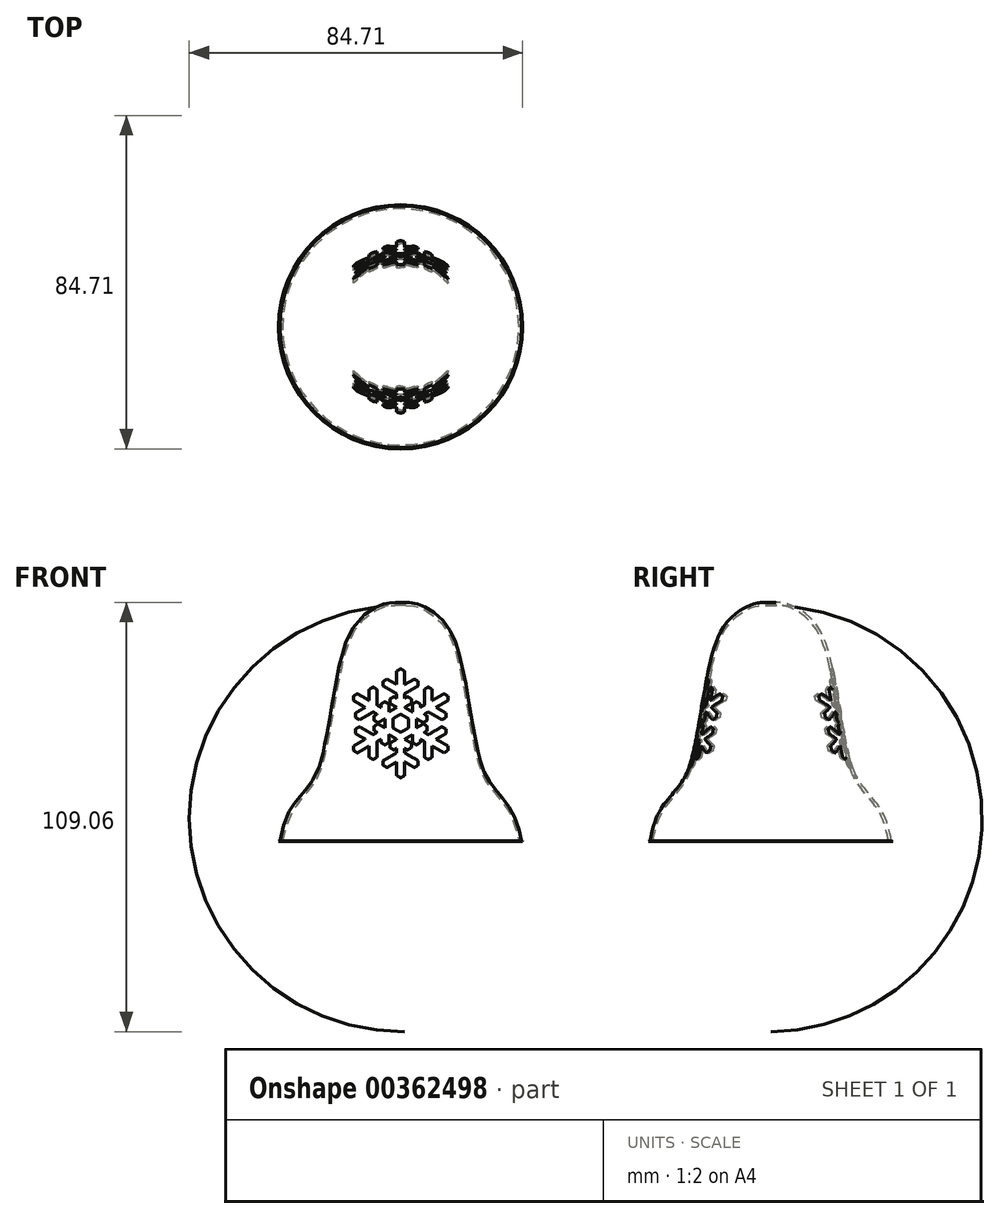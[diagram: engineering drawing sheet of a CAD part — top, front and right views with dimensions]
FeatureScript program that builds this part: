
annotation { "Feature Type Name" : "Feature", "Feature Type Description" : "" }
export const myFeature = defineFeature(function(context is Context, id is Id, definition is map)
    precondition{}
    {
        {
            var Q0;
            Q0=qCreatedBy(makeId("Front.planeOp"),FACE);
            var sketch = newSketch(context, id + "F0", { "sketchPlane" : qUnion([Q0])});
            skLineSegment(sketch, "E0", {"start": v(0, 60.7) * mm, "end": v(0, 0) * mm});
            skLineSegment(sketch, "E1", {"start": v(0, 0) * mm, "end": v(31, 0) * mm});
            skFitSpline(sketch, "E2", {"points": [v(0, 60) * mm, v(4.46, 59.52) * mm, v(9.31, 56.54) * mm, v(14.11, 47.63) * mm, v(19.42, 20.89) * mm, v(23, 13.4) * mm, v(27.43, 7.62) * mm, v(30, 0) * mm], "startDerivative": vector(62.73, 0.31) * mm, "endDerivative": vector(16.94, -75.2) * mm});
            skFitSpline(sketch, "E3.0", {"points": [v(0, 59.5) * mm, v(0.65, 59.5) * mm, v(1.75, 59.5) * mm, v(2.78, 59.42) * mm, v(3.52, 59.28) * mm, v(4.08, 59.13) * mm, v(4.68, 58.91) * mm, v(5.53, 58.55) * mm, v(6.65, 57.95) * mm, v(7.79, 57.18) * mm, v(8.65, 56.47) * mm, v(9.48, 55.71) * mm, v(10.42, 54.66) * mm, v(11.44, 53.13) * mm, v(12.36, 51.27) * mm, v(13.07, 49.37) * mm, v(13.6, 47.61) * mm, v(14.12, 45.67) * mm, v(14.74, 42.95) * mm, v(15.66, 38.18) * mm, v(16.53, 33.06) * mm, v(17.38, 28.15) * mm, v(17.92, 25.29) * mm, v(18.35, 23.2) * mm, v(18.69, 21.73) * mm, v(19.03, 20.4) * mm, v(19.5, 18.82) * mm, v(20.12, 17.15) * mm, v(20.95, 15.49) * mm, v(21.72, 14.28) * mm, v(22.4, 13.36) * mm, v(23.12, 12.44) * mm, v(24.08, 11.28) * mm, v(25.25, 9.86) * mm, v(26.16, 8.67) * mm, v(26.8, 7.72) * mm, v(27.37, 6.76) * mm, v(27.94, 5.54) * mm, v(28.5, 3.94) * mm, v(29, 2.1) * mm, v(29.34, 0.67) * mm, v(29.51, -0.1) * mm]});
            skFitSpline(sketch, "E4.0", {"points": [v(0, 60.7) * mm, v(0.65, 60.7) * mm, v(1.77, 60.7) * mm, v(2.92, 60.61) * mm, v(3.8, 60.45) * mm, v(4.45, 60.27) * mm, v(5.12, 60.03) * mm, v(6.06, 59.63) * mm, v(7.28, 58.98) * mm, v(8.74, 57.98) * mm, v(10.13, 56.78) * mm, v(11.37, 55.4) * mm, v(12.48, 53.73) * mm, v(13.47, 51.74) * mm, v(14.2, 49.76) * mm, v(14.76, 47.94) * mm, v(15.29, 45.95) * mm, v(15.91, 43.2) * mm, v(16.84, 38.39) * mm, v(17.71, 33.26) * mm, v(18.56, 28.36) * mm, v(19.1, 25.52) * mm, v(19.53, 23.45) * mm, v(19.85, 22.02) * mm, v(20.19, 20.72) * mm, v(20.64, 19.2) * mm, v(21.23, 17.62) * mm, v(22, 16.08) * mm, v(22.7, 14.96) * mm, v(23.35, 14.09) * mm, v(24.05, 13.2) * mm, v(25, 12.05) * mm, v(26.19, 10.62) * mm, v(27.32, 9.13) * mm, v(28.3, 7.59) * mm, v(29.06, 6) * mm, v(29.86, 3.72) * mm, v(30.33, 1.72) * mm, v(30.68, 0.15) * mm]});
            skLineSegment(sketch, "E5", {"start": v(30.68, 0.15) * mm, "end": v(31, 0) * mm});
            skLineSegment(sketch, "E6", {"start": v(0, 59.5) * mm, "end": v(0, 59.5) * mm});
            skLineSegment(sketch, "E7.0", {"start": v(1.4, 60.7) * mm, "end": v(1.4, 0) * mm});
            skSolve(sketch);
        }
        {
            var Q0;
            Q0=qCreatedBy(makeId("Front.planeOp"),FACE);
            var sketch = newSketch(context, id + "F1", { "sketchPlane" : qUnion([Q0])});
            skLineSegment(sketch, "E8", {"start": v(0, 0) * mm, "end": v(0, 54.78) * mm, "construction": true});
            skLineSegment(sketch, "E9", {"start": v(-27.16, 30) * mm, "end": v(27.16, 30) * mm, "construction": true});
            skPoint(sketch, "E10", {"position": v(0, 30) * mm});
            skCircle(sketch, "E11.cCircle", {"center": v(0, 30) * mm, "radius": 12 * mm, "construction": true});
            skLineSegment(sketch, "E11.0", {"start": v(-12, 23.07) * mm, "end": v(-12, 36.93) * mm, "construction": true});
            skLineSegment(sketch, "E11.1", {"start": v(-12, 36.93) * mm, "end": v(0, 43.86) * mm, "construction": true});
            skLineSegment(sketch, "E11.2", {"start": v(0, 43.86) * mm, "end": v(12, 36.93) * mm, "construction": true});
            skLineSegment(sketch, "E11.3", {"start": v(12, 36.93) * mm, "end": v(12, 23.07) * mm, "construction": true});
            skLineSegment(sketch, "E11.4", {"start": v(12, 23.07) * mm, "end": v(0, 16.14) * mm, "construction": true});
            skLineSegment(sketch, "E11.5", {"start": v(0, 16.14) * mm, "end": v(-12, 23.07) * mm, "construction": true});
            skPoint(sketch, "E11.0.midPoint", {"position": v(-12, 30) * mm});
            skCircle(sketch, "E12.cCircle", {"center": v(0, 30) * mm, "radius": 2 * mm, "construction": true});
            skLineSegment(sketch, "E12.0", {"start": v(-2, 28.85) * mm, "end": v(-2, 31.15) * mm});
            skLineSegment(sketch, "E12.1", {"start": v(-2, 31.15) * mm, "end": v(0, 32.3) * mm});
            skLineSegment(sketch, "E12.2", {"start": v(0, 32.3) * mm, "end": v(2, 31.15) * mm});
            skLineSegment(sketch, "E12.3", {"start": v(2, 31.15) * mm, "end": v(2, 28.85) * mm});
            skLineSegment(sketch, "E12.4", {"start": v(2, 28.85) * mm, "end": v(0, 27.7) * mm});
            skLineSegment(sketch, "E12.5", {"start": v(0, 27.7) * mm, "end": v(-2, 28.85) * mm});
            skPoint(sketch, "E12.0.midPoint", {"position": v(-2, 30) * mm});
            skPoint(sketch, "E13.0.midPoint", {"position": v(-4, 30) * mm});
            skPoint(sketch, "E14.start.orphan", {"position": v(-1, 30) * mm});
            skLineSegment(sketch, "E15.trimOffspring", {"start": v(1, 36.35) * mm, "end": v(1, 37.5) * mm});
            skPoint(sketch, "E16.MirrorCS.start.orphan", {"position": v(1, 30) * mm});
            skPoint(sketch, "E17.orphan", {"position": v(0, 34.62) * mm});
            skLineSegment(sketch, "E18", {"start": v(1, 43.28) * mm, "end": v(0, 43.86) * mm});
            skPoint(sketch, "E19", {"position": v(1, 38.66) * mm});
            skLineSegment(sketch, "E20", {"start": v(1, 39.81) * mm, "end": v(1, 43.28) * mm});
            skLineSegment(sketch, "E21", {"start": v(1, 38.66) * mm, "end": v(4.46, 40.66) * mm, "construction": true});
            skLineSegment(sketch, "E22", {"start": v(1, 34.04) * mm, "end": v(2.73, 35.04) * mm});
            skLineSegment(sketch, "E23.0", {"start": v(1, 37.5) * mm, "end": v(4.46, 39.5) * mm});
            skLineSegment(sketch, "E24.MirrorCS", {"start": v(1, 39.81) * mm, "end": v(3.46, 41.24) * mm});
            skLineSegment(sketch, "E25", {"start": v(4.46, 39.5) * mm, "end": v(4.46, 40.66) * mm});
            skLineSegment(sketch, "E26", {"start": v(4.46, 40.66) * mm, "end": v(3.46, 41.24) * mm});
            skPoint(sketch, "E27.orphan", {"position": v(6.75, 38.52) * mm});
            skLineSegment(sketch, "E28", {"start": v(1, 35.2) * mm, "end": v(2.73, 36.2) * mm, "construction": true});
            skLineSegment(sketch, "E29.MirrorCS", {"start": v(1, 36.35) * mm, "end": v(1.73, 36.77) * mm});
            skLineSegment(sketch, "E30", {"start": v(1.73, 36.77) * mm, "end": v(2.73, 36.2) * mm});
            skLineSegment(sketch, "E31", {"start": v(2.73, 36.2) * mm, "end": v(2.73, 35.04) * mm});
            skLineSegment(sketch, "E32.MirrorCS", {"start": v(-1, 36.35) * mm, "end": v(-1.73, 36.77) * mm});
            skLineSegment(sketch, "E33.MirrorCS", {"start": v(-1, 39.81) * mm, "end": v(-3.46, 41.24) * mm});
            skLineSegment(sketch, "E34.MirrorCS", {"start": v(-4.46, 39.5) * mm, "end": v(-4.46, 40.66) * mm});
            skLineSegment(sketch, "E35.MirrorCS", {"start": v(-1, 39.81) * mm, "end": v(-1, 43.28) * mm});
            skLineSegment(sketch, "E36.MirrorCS", {"start": v(-1, 34.04) * mm, "end": v(-2.73, 35.04) * mm});
            skLineSegment(sketch, "E37.MirrorCS", {"start": v(-2.73, 36.2) * mm, "end": v(-2.73, 35.04) * mm});
            skLineSegment(sketch, "E38.MirrorCS", {"start": v(-1, 38.66) * mm, "end": v(-4.46, 40.66) * mm, "construction": true});
            skLineSegment(sketch, "E39.MirrorCS", {"start": v(-1, 43.28) * mm, "end": v(0, 43.86) * mm});
            skLineSegment(sketch, "E40.MirrorCS", {"start": v(-1, 36.35) * mm, "end": v(-1, 37.5) * mm});
            skLineSegment(sketch, "E41.MirrorCS", {"start": v(-4.46, 40.66) * mm, "end": v(-3.46, 41.24) * mm});
            skLineSegment(sketch, "E42.MirrorCS", {"start": v(-1.73, 36.77) * mm, "end": v(-2.73, 36.2) * mm});
            skLineSegment(sketch, "E43.MirrorCS", {"start": v(-1, 35.2) * mm, "end": v(-2.73, 36.2) * mm, "construction": true});
            skPoint(sketch, "E44.MirrorP", {"position": v(-1, 38.66) * mm});
            skLineSegment(sketch, "E45.MirrorCS", {"start": v(-1, 37.5) * mm, "end": v(-4.46, 39.5) * mm});
            skLineSegment(sketch, "E46.1.0", {"start": v(-11, 37.5) * mm, "end": v(-12, 36.93) * mm});
            skLineSegment(sketch, "E46.1.1", {"start": v(-3, 32.89) * mm, "end": v(-3, 34.89) * mm});
            skLineSegment(sketch, "E46.1.2", {"start": v(-7, 32.89) * mm, "end": v(-10.46, 30.89) * mm});
            skLineSegment(sketch, "E46.1.3", {"start": v(-11.46, 31.46) * mm, "end": v(-11.46, 32.62) * mm});
            skLineSegment(sketch, "E46.1.4", {"start": v(-4, 35.46) * mm, "end": v(-3, 34.89) * mm});
            skLineSegment(sketch, "E46.1.5", {"start": v(-6.73, 30.73) * mm, "end": v(-5.73, 30.15) * mm});
            skPoint(sketch, "E46.1.6", {"position": v(-7, 35.2) * mm});
            skLineSegment(sketch, "E46.1.7", {"start": v(-9, 34.04) * mm, "end": v(-12, 35.77) * mm});
            skLineSegment(sketch, "E46.1.8", {"start": v(-4, 31.15) * mm, "end": v(-5.73, 30.15) * mm});
            skPoint(sketch, "E46.1.9", {"position": v(-4, 32.3) * mm});
            skPoint(sketch, "E46.1.10", {"position": v(-8, 33.46) * mm});
            skLineSegment(sketch, "E46.1.11", {"start": v(-7, 39.2) * mm, "end": v(-8, 38.62) * mm});
            skLineSegment(sketch, "E46.1.12", {"start": v(-5, 34.04) * mm, "end": v(-6, 34.62) * mm});
            skLineSegment(sketch, "E46.1.13", {"start": v(-9, 34.04) * mm, "end": v(-11.46, 32.62) * mm});
            skLineSegment(sketch, "E46.1.14", {"start": v(-8, 35.77) * mm, "end": v(-11, 37.5) * mm});
            skLineSegment(sketch, "E46.1.15", {"start": v(-6.73, 31.89) * mm, "end": v(-6.73, 30.73) * mm});
            skLineSegment(sketch, "E46.1.16", {"start": v(-6, 38.62) * mm, "end": v(-7, 39.2) * mm});
            skLineSegment(sketch, "E46.1.17", {"start": v(-5, 34.89) * mm, "end": v(-4, 35.46) * mm});
            skLineSegment(sketch, "E46.1.18", {"start": v(-4, 33.46) * mm, "end": v(-4, 35.46) * mm, "construction": true});
            skLineSegment(sketch, "E46.1.19", {"start": v(-10.46, 30.89) * mm, "end": v(-11.46, 31.46) * mm});
            skLineSegment(sketch, "E46.1.20", {"start": v(-8, 35.77) * mm, "end": v(-8, 38.62) * mm});
            skLineSegment(sketch, "E46.1.21", {"start": v(-12, 35.77) * mm, "end": v(-12, 36.93) * mm});
            skLineSegment(sketch, "E46.1.22", {"start": v(-6, 32.3) * mm, "end": v(-7, 32.89) * mm});
            skLineSegment(sketch, "E46.1.23", {"start": v(-5, 31.73) * mm, "end": v(-6.73, 30.73) * mm, "construction": true});
            skLineSegment(sketch, "E46.1.24", {"start": v(-8, 33.46) * mm, "end": v(-11.46, 31.46) * mm, "construction": true});
            skLineSegment(sketch, "E46.1.25", {"start": v(-7, 35.2) * mm, "end": v(-7, 39.2) * mm, "construction": true});
            skLineSegment(sketch, "E46.1.26", {"start": v(-6, 34.62) * mm, "end": v(-6, 38.62) * mm});
            skPoint(sketch, "E46.1.27", {"position": v(-4, 32.3) * mm});
            skLineSegment(sketch, "E46.1.28", {"start": v(-6, 32.3) * mm, "end": v(-6.73, 31.89) * mm});
            skLineSegment(sketch, "E46.1.29", {"start": v(-5, 34.04) * mm, "end": v(-5, 34.89) * mm});
            skLineSegment(sketch, "E46.2.0", {"start": v(-12, 24.23) * mm, "end": v(-12, 23.07) * mm});
            skLineSegment(sketch, "E46.2.1", {"start": v(-4, 28.85) * mm, "end": v(-5.73, 29.85) * mm});
            skLineSegment(sketch, "E46.2.2", {"start": v(-6, 25.38) * mm, "end": v(-6, 21.38) * mm});
            skLineSegment(sketch, "E46.2.3", {"start": v(-7, 20.8) * mm, "end": v(-8, 21.38) * mm});
            skLineSegment(sketch, "E46.2.4", {"start": v(-6.73, 29.27) * mm, "end": v(-5.73, 29.85) * mm});
            skLineSegment(sketch, "E46.2.5", {"start": v(-4, 24.54) * mm, "end": v(-3, 25.11) * mm});
            skPoint(sketch, "E46.2.6", {"position": v(-8, 26.54) * mm});
            skLineSegment(sketch, "E46.2.7", {"start": v(-8, 24.23) * mm, "end": v(-11, 22.5) * mm});
            skLineSegment(sketch, "E46.2.8", {"start": v(-3, 27.11) * mm, "end": v(-3, 25.11) * mm});
            skPoint(sketch, "E46.2.9", {"position": v(-4, 27.7) * mm});
            skPoint(sketch, "E46.2.10", {"position": v(-7, 24.8) * mm});
            skLineSegment(sketch, "E46.2.11", {"start": v(-11.46, 28.54) * mm, "end": v(-11.46, 27.38) * mm});
            skLineSegment(sketch, "E46.2.12", {"start": v(-6, 27.7) * mm, "end": v(-7, 27.11) * mm});
            skLineSegment(sketch, "E46.2.13", {"start": v(-8, 24.23) * mm, "end": v(-8, 21.38) * mm});
            skLineSegment(sketch, "E46.2.14", {"start": v(-9, 25.96) * mm, "end": v(-12, 24.23) * mm});
            skLineSegment(sketch, "E46.2.15", {"start": v(-5, 25.11) * mm, "end": v(-4, 24.54) * mm});
            skLineSegment(sketch, "E46.2.16", {"start": v(-10.46, 29.11) * mm, "end": v(-11.46, 28.54) * mm});
            skLineSegment(sketch, "E46.2.17", {"start": v(-6.73, 28.11) * mm, "end": v(-6.73, 29.27) * mm});
            skLineSegment(sketch, "E46.2.18", {"start": v(-5, 28.27) * mm, "end": v(-6.73, 29.27) * mm, "construction": true});
            skLineSegment(sketch, "E46.2.19", {"start": v(-6, 21.38) * mm, "end": v(-7, 20.8) * mm});
            skLineSegment(sketch, "E46.2.20", {"start": v(-9, 25.96) * mm, "end": v(-11.46, 27.38) * mm});
            skLineSegment(sketch, "E46.2.21", {"start": v(-11, 22.5) * mm, "end": v(-12, 23.07) * mm});
            skLineSegment(sketch, "E46.2.22", {"start": v(-5, 25.96) * mm, "end": v(-6, 25.38) * mm});
            skLineSegment(sketch, "E46.2.23", {"start": v(-4, 26.54) * mm, "end": v(-4, 24.54) * mm, "construction": true});
            skLineSegment(sketch, "E46.2.24", {"start": v(-7, 24.8) * mm, "end": v(-7, 20.8) * mm, "construction": true});
            skLineSegment(sketch, "E46.2.25", {"start": v(-8, 26.54) * mm, "end": v(-11.46, 28.54) * mm, "construction": true});
            skLineSegment(sketch, "E46.2.26", {"start": v(-7, 27.11) * mm, "end": v(-10.46, 29.11) * mm});
            skPoint(sketch, "E46.2.27", {"position": v(-4, 27.7) * mm});
            skLineSegment(sketch, "E46.2.28", {"start": v(-5, 25.96) * mm, "end": v(-5, 25.11) * mm});
            skLineSegment(sketch, "E46.2.29", {"start": v(-6, 27.7) * mm, "end": v(-6.73, 28.11) * mm});
            skLineSegment(sketch, "E46.3.0", {"start": v(-1, 16.72) * mm, "end": v(0, 16.14) * mm});
            skLineSegment(sketch, "E46.3.1", {"start": v(-1, 25.96) * mm, "end": v(-2.73, 24.96) * mm});
            skLineSegment(sketch, "E46.3.2", {"start": v(1, 22.5) * mm, "end": v(4.46, 20.5) * mm});
            skLineSegment(sketch, "E46.3.3", {"start": v(4.46, 19.34) * mm, "end": v(3.46, 18.76) * mm});
            skLineSegment(sketch, "E46.3.4", {"start": v(-2.73, 23.8) * mm, "end": v(-2.73, 24.96) * mm});
            skLineSegment(sketch, "E46.3.5", {"start": v(2.73, 23.8) * mm, "end": v(2.73, 24.96) * mm});
            skPoint(sketch, "E46.3.6", {"position": v(-1, 21.34) * mm});
            skLineSegment(sketch, "E46.3.7", {"start": v(1, 20.19) * mm, "end": v(1, 16.72) * mm});
            skLineSegment(sketch, "E46.3.8", {"start": v(1, 25.96) * mm, "end": v(2.73, 24.96) * mm});
            skPoint(sketch, "E46.3.9", {"position": v(0, 25.38) * mm});
            skPoint(sketch, "E46.3.10", {"position": v(1, 21.34) * mm});
            skLineSegment(sketch, "E46.3.11", {"start": v(-4.46, 19.34) * mm, "end": v(-3.46, 18.76) * mm});
            skLineSegment(sketch, "E46.3.12", {"start": v(-1, 23.65) * mm, "end": v(-1, 22.5) * mm});
            skLineSegment(sketch, "E46.3.13", {"start": v(1, 20.19) * mm, "end": v(3.46, 18.76) * mm});
            skLineSegment(sketch, "E46.3.14", {"start": v(-1, 20.19) * mm, "end": v(-1, 16.72) * mm});
            skLineSegment(sketch, "E46.3.15", {"start": v(1.73, 23.23) * mm, "end": v(2.73, 23.8) * mm});
            skLineSegment(sketch, "E46.3.16", {"start": v(-4.46, 20.5) * mm, "end": v(-4.46, 19.34) * mm});
            skLineSegment(sketch, "E46.3.17", {"start": v(-1.73, 23.23) * mm, "end": v(-2.73, 23.8) * mm});
            skLineSegment(sketch, "E46.3.18", {"start": v(-1, 24.8) * mm, "end": v(-2.73, 23.8) * mm, "construction": true});
            skLineSegment(sketch, "E46.3.19", {"start": v(4.46, 20.5) * mm, "end": v(4.46, 19.34) * mm});
            skLineSegment(sketch, "E46.3.20", {"start": v(-1, 20.19) * mm, "end": v(-3.46, 18.76) * mm});
            skLineSegment(sketch, "E46.3.21", {"start": v(1, 16.72) * mm, "end": v(0, 16.14) * mm});
            skLineSegment(sketch, "E46.3.22", {"start": v(1, 23.65) * mm, "end": v(1, 22.5) * mm});
            skLineSegment(sketch, "E46.3.23", {"start": v(1, 24.8) * mm, "end": v(2.73, 23.8) * mm, "construction": true});
            skLineSegment(sketch, "E46.3.24", {"start": v(1, 21.34) * mm, "end": v(4.46, 19.34) * mm, "construction": true});
            skLineSegment(sketch, "E46.3.25", {"start": v(-1, 21.34) * mm, "end": v(-4.46, 19.34) * mm, "construction": true});
            skLineSegment(sketch, "E46.3.26", {"start": v(-1, 22.5) * mm, "end": v(-4.46, 20.5) * mm});
            skPoint(sketch, "E46.3.27", {"position": v(0, 25.38) * mm});
            skLineSegment(sketch, "E46.3.28", {"start": v(1, 23.65) * mm, "end": v(1.73, 23.23) * mm});
            skLineSegment(sketch, "E46.3.29", {"start": v(-1, 23.65) * mm, "end": v(-1.73, 23.23) * mm});
            skLineSegment(sketch, "E46.4.0", {"start": v(11, 22.5) * mm, "end": v(12, 23.07) * mm});
            skLineSegment(sketch, "E46.4.1", {"start": v(3, 27.11) * mm, "end": v(3, 25.11) * mm});
            skLineSegment(sketch, "E46.4.2", {"start": v(7, 27.11) * mm, "end": v(10.46, 29.11) * mm});
            skLineSegment(sketch, "E46.4.3", {"start": v(11.46, 28.54) * mm, "end": v(11.46, 27.38) * mm});
            skLineSegment(sketch, "E46.4.4", {"start": v(4, 24.54) * mm, "end": v(3, 25.11) * mm});
            skLineSegment(sketch, "E46.4.5", {"start": v(6.73, 29.27) * mm, "end": v(5.73, 29.85) * mm});
            skPoint(sketch, "E46.4.6", {"position": v(7, 24.8) * mm});
            skLineSegment(sketch, "E46.4.7", {"start": v(9, 25.96) * mm, "end": v(12, 24.23) * mm});
            skLineSegment(sketch, "E46.4.8", {"start": v(4, 28.85) * mm, "end": v(5.73, 29.85) * mm});
            skPoint(sketch, "E46.4.9", {"position": v(4, 27.7) * mm});
            skPoint(sketch, "E46.4.10", {"position": v(8, 26.54) * mm});
            skLineSegment(sketch, "E46.4.11", {"start": v(7, 20.8) * mm, "end": v(8, 21.38) * mm});
            skLineSegment(sketch, "E46.4.12", {"start": v(5, 25.96) * mm, "end": v(6, 25.38) * mm});
            skLineSegment(sketch, "E46.4.13", {"start": v(9, 25.96) * mm, "end": v(11.46, 27.38) * mm});
            skLineSegment(sketch, "E46.4.14", {"start": v(8, 24.23) * mm, "end": v(11, 22.5) * mm});
            skLineSegment(sketch, "E46.4.15", {"start": v(6.73, 28.11) * mm, "end": v(6.73, 29.27) * mm});
            skLineSegment(sketch, "E46.4.16", {"start": v(6, 21.38) * mm, "end": v(7, 20.8) * mm});
            skLineSegment(sketch, "E46.4.17", {"start": v(5, 25.11) * mm, "end": v(4, 24.54) * mm});
            skLineSegment(sketch, "E46.4.18", {"start": v(4, 26.54) * mm, "end": v(4, 24.54) * mm, "construction": true});
            skLineSegment(sketch, "E46.4.19", {"start": v(10.46, 29.11) * mm, "end": v(11.46, 28.54) * mm});
            skLineSegment(sketch, "E46.4.20", {"start": v(8, 24.23) * mm, "end": v(8, 21.38) * mm});
            skLineSegment(sketch, "E46.4.21", {"start": v(12, 24.23) * mm, "end": v(12, 23.07) * mm});
            skLineSegment(sketch, "E46.4.22", {"start": v(6, 27.7) * mm, "end": v(7, 27.11) * mm});
            skLineSegment(sketch, "E46.4.23", {"start": v(5, 28.27) * mm, "end": v(6.73, 29.27) * mm, "construction": true});
            skLineSegment(sketch, "E46.4.24", {"start": v(8, 26.54) * mm, "end": v(11.46, 28.54) * mm, "construction": true});
            skLineSegment(sketch, "E46.4.25", {"start": v(7, 24.8) * mm, "end": v(7, 20.8) * mm, "construction": true});
            skLineSegment(sketch, "E46.4.26", {"start": v(6, 25.38) * mm, "end": v(6, 21.38) * mm});
            skPoint(sketch, "E46.4.27", {"position": v(4, 27.7) * mm});
            skLineSegment(sketch, "E46.4.28", {"start": v(6, 27.7) * mm, "end": v(6.73, 28.11) * mm});
            skLineSegment(sketch, "E46.4.29", {"start": v(5, 25.96) * mm, "end": v(5, 25.11) * mm});
            skLineSegment(sketch, "E46.5.0", {"start": v(12, 35.77) * mm, "end": v(12, 36.93) * mm});
            skLineSegment(sketch, "E46.5.1", {"start": v(4, 31.15) * mm, "end": v(5.73, 30.15) * mm});
            skLineSegment(sketch, "E46.5.2", {"start": v(6, 34.62) * mm, "end": v(6, 38.62) * mm});
            skLineSegment(sketch, "E46.5.3", {"start": v(7, 39.2) * mm, "end": v(8, 38.62) * mm});
            skLineSegment(sketch, "E46.5.4", {"start": v(6.73, 30.73) * mm, "end": v(5.73, 30.15) * mm});
            skLineSegment(sketch, "E46.5.5", {"start": v(4, 35.46) * mm, "end": v(3, 34.89) * mm});
            skPoint(sketch, "E46.5.6", {"position": v(8, 33.46) * mm});
            skLineSegment(sketch, "E46.5.7", {"start": v(8, 35.77) * mm, "end": v(11, 37.5) * mm});
            skLineSegment(sketch, "E46.5.8", {"start": v(3, 32.89) * mm, "end": v(3, 34.89) * mm});
            skPoint(sketch, "E46.5.9", {"position": v(4, 32.3) * mm});
            skPoint(sketch, "E46.5.10", {"position": v(7, 35.2) * mm});
            skLineSegment(sketch, "E46.5.11", {"start": v(11.46, 31.46) * mm, "end": v(11.46, 32.62) * mm});
            skLineSegment(sketch, "E46.5.12", {"start": v(6, 32.3) * mm, "end": v(7, 32.89) * mm});
            skLineSegment(sketch, "E46.5.13", {"start": v(8, 35.77) * mm, "end": v(8, 38.62) * mm});
            skLineSegment(sketch, "E46.5.14", {"start": v(9, 34.04) * mm, "end": v(12, 35.77) * mm});
            skLineSegment(sketch, "E46.5.15", {"start": v(5, 34.89) * mm, "end": v(4, 35.46) * mm});
            skLineSegment(sketch, "E46.5.16", {"start": v(10.46, 30.89) * mm, "end": v(11.46, 31.46) * mm});
            skLineSegment(sketch, "E46.5.17", {"start": v(6.73, 31.89) * mm, "end": v(6.73, 30.73) * mm});
            skLineSegment(sketch, "E46.5.18", {"start": v(5, 31.73) * mm, "end": v(6.73, 30.73) * mm, "construction": true});
            skLineSegment(sketch, "E46.5.19", {"start": v(6, 38.62) * mm, "end": v(7, 39.2) * mm});
            skLineSegment(sketch, "E46.5.20", {"start": v(9, 34.04) * mm, "end": v(11.46, 32.62) * mm});
            skLineSegment(sketch, "E46.5.21", {"start": v(11, 37.5) * mm, "end": v(12, 36.93) * mm});
            skLineSegment(sketch, "E46.5.22", {"start": v(5, 34.04) * mm, "end": v(6, 34.62) * mm});
            skLineSegment(sketch, "E46.5.23", {"start": v(4, 33.46) * mm, "end": v(4, 35.46) * mm, "construction": true});
            skLineSegment(sketch, "E46.5.24", {"start": v(7, 35.2) * mm, "end": v(7, 39.2) * mm, "construction": true});
            skLineSegment(sketch, "E46.5.25", {"start": v(8, 33.46) * mm, "end": v(11.46, 31.46) * mm, "construction": true});
            skLineSegment(sketch, "E46.5.26", {"start": v(7, 32.89) * mm, "end": v(10.46, 30.89) * mm});
            skPoint(sketch, "E46.5.27", {"position": v(4, 32.3) * mm});
            skLineSegment(sketch, "E46.5.28", {"start": v(5, 34.04) * mm, "end": v(5, 34.89) * mm});
            skLineSegment(sketch, "E46.5.29", {"start": v(6, 32.3) * mm, "end": v(6.73, 31.89) * mm});
            skLineSegment(sketch, "E47", {"start": v(-3, 32.89) * mm, "end": v(-1, 34.04) * mm});
            skLineSegment(sketch, "E48", {"start": v(1, 34.04) * mm, "end": v(3, 32.89) * mm});
            skLineSegment(sketch, "E49", {"start": v(4, 31.15) * mm, "end": v(4, 28.85) * mm});
            skLineSegment(sketch, "E50", {"start": v(3, 27.11) * mm, "end": v(1, 25.96) * mm});
            skLineSegment(sketch, "E51", {"start": v(-1, 25.96) * mm, "end": v(-3, 27.11) * mm});
            skLineSegment(sketch, "E52", {"start": v(-4, 28.85) * mm, "end": v(-4, 31.15) * mm});
            skSolve(sketch);
        }
        {
            var Q0;
            {var subQ0=sQuery(id+"F0.wireOp",EDGE,"E5");Q0=makeQuery(id+"F0.imprint","IMPRINT",FACE,{"disambiguationData":[TD([[makeQuery(id+"F0.imprint","IMPRINT",EDGE,{"derivedFrom":subQ0}),-1.0]])]});}
            var Q1;
            Q1=sQuery(id+"F0.wireOp",EDGE,"E0");
            revolve(context, id + "F2", {"entities" : qUnion([Q0]), "axis" : qUnion([Q1]), "revolveType" : RevolveType.FULL});
        }
        {
            var Q0;
            Q0=makeQuery(id+"F1.imprint","IMPRINT",FACE,{"disambiguationData":[TD([[makeQuery(id+"F1.imprint","IMPRINT",EDGE,{"derivedFrom":sQuery(id+"F1.wireOp",EDGE,"E12.0")}),1.0]])]});
            extrude(context, id + "F3", {"entities" : qUnion([Q0]), "endBound" : BoundingType.SYMMETRIC, "depth" : 100 * mm});
        }
        {
            var Q0;
            Q0=makeQuery(id+"F2.opRevolve","SWEPT_BODY",BODY,{"disambiguationData":[OSD([sQuery(id+"F0.wireOp",EDGE,"E1"),sQuery(id+"F0.wireOp",EDGE,"E2"),sQuery(id+"F0.wireOp",EDGE,"E4.0"),sQuery(id+"F0.wireOp",EDGE,"E5"),sQuery(id+"F0.wireOp",EDGE,"E7.0")])]});
            var Q1;
            Q1=makeQuery(id+"F3.opExtrude","SWEPT_BODY",BODY,{"disambiguationData":[OSD([sQuery(id+"F1.wireOp",EDGE,"E12.0"),sQuery(id+"F1.wireOp",EDGE,"E12.1"),sQuery(id+"F1.wireOp",EDGE,"E12.2"),sQuery(id+"F1.wireOp",EDGE,"E12.3"),sQuery(id+"F1.wireOp",EDGE,"E12.4"),sQuery(id+"F1.wireOp",EDGE,"E12.5"),sQuery(id+"F1.wireOp",EDGE,"E15.trimOffspring"),sQuery(id+"F1.wireOp",EDGE,"E18"),sQuery(id+"F1.wireOp",EDGE,"E20"),sQuery(id+"F1.wireOp",EDGE,"E22"),sQuery(id+"F1.wireOp",EDGE,"E23.0"),sQuery(id+"F1.wireOp",EDGE,"E24.MirrorCS"),sQuery(id+"F1.wireOp",EDGE,"E25"),sQuery(id+"F1.wireOp",EDGE,"E26"),sQuery(id+"F1.wireOp",EDGE,"E29.MirrorCS"),sQuery(id+"F1.wireOp",EDGE,"E30"),sQuery(id+"F1.wireOp",EDGE,"E31"),sQuery(id+"F1.wireOp",EDGE,"E32.MirrorCS"),sQuery(id+"F1.wireOp",EDGE,"E33.MirrorCS"),sQuery(id+"F1.wireOp",EDGE,"E34.MirrorCS"),sQuery(id+"F1.wireOp",EDGE,"E35.MirrorCS"),sQuery(id+"F1.wireOp",EDGE,"E36.MirrorCS"),sQuery(id+"F1.wireOp",EDGE,"E37.MirrorCS"),sQuery(id+"F1.wireOp",EDGE,"E39.MirrorCS"),sQuery(id+"F1.wireOp",EDGE,"E40.MirrorCS"),sQuery(id+"F1.wireOp",EDGE,"E41.MirrorCS"),sQuery(id+"F1.wireOp",EDGE,"E42.MirrorCS"),sQuery(id+"F1.wireOp",EDGE,"E45.MirrorCS"),sQuery(id+"F1.wireOp",EDGE,"E46.1.0"),sQuery(id+"F1.wireOp",EDGE,"E46.1.1"),sQuery(id+"F1.wireOp",EDGE,"E46.1.2"),sQuery(id+"F1.wireOp",EDGE,"E46.1.3"),sQuery(id+"F1.wireOp",EDGE,"E46.1.4"),sQuery(id+"F1.wireOp",EDGE,"E46.1.5"),sQuery(id+"F1.wireOp",EDGE,"E46.1.7"),sQuery(id+"F1.wireOp",EDGE,"E46.1.8"),sQuery(id+"F1.wireOp",EDGE,"E46.1.11"),sQuery(id+"F1.wireOp",EDGE,"E46.1.12"),sQuery(id+"F1.wireOp",EDGE,"E46.1.13"),sQuery(id+"F1.wireOp",EDGE,"E46.1.14"),sQuery(id+"F1.wireOp",EDGE,"E46.1.15"),sQuery(id+"F1.wireOp",EDGE,"E46.1.16"),sQuery(id+"F1.wireOp",EDGE,"E46.1.17"),sQuery(id+"F1.wireOp",EDGE,"E46.1.19"),sQuery(id+"F1.wireOp",EDGE,"E46.1.20"),sQuery(id+"F1.wireOp",EDGE,"E46.1.21"),sQuery(id+"F1.wireOp",EDGE,"E46.1.22"),sQuery(id+"F1.wireOp",EDGE,"E46.1.26"),sQuery(id+"F1.wireOp",EDGE,"E46.1.28"),sQuery(id+"F1.wireOp",EDGE,"E46.1.29"),sQuery(id+"F1.wireOp",EDGE,"E46.2.0"),sQuery(id+"F1.wireOp",EDGE,"E46.2.1"),sQuery(id+"F1.wireOp",EDGE,"E46.2.2"),sQuery(id+"F1.wireOp",EDGE,"E46.2.3"),sQuery(id+"F1.wireOp",EDGE,"E46.2.4"),sQuery(id+"F1.wireOp",EDGE,"E46.2.5"),sQuery(id+"F1.wireOp",EDGE,"E46.2.7"),sQuery(id+"F1.wireOp",EDGE,"E46.2.8"),sQuery(id+"F1.wireOp",EDGE,"E46.2.11"),sQuery(id+"F1.wireOp",EDGE,"E46.2.12"),sQuery(id+"F1.wireOp",EDGE,"E46.2.13"),sQuery(id+"F1.wireOp",EDGE,"E46.2.14"),sQuery(id+"F1.wireOp",EDGE,"E46.2.15"),sQuery(id+"F1.wireOp",EDGE,"E46.2.16"),sQuery(id+"F1.wireOp",EDGE,"E46.2.17"),sQuery(id+"F1.wireOp",EDGE,"E46.2.19"),sQuery(id+"F1.wireOp",EDGE,"E46.2.20"),sQuery(id+"F1.wireOp",EDGE,"E46.2.21"),sQuery(id+"F1.wireOp",EDGE,"E46.2.22"),sQuery(id+"F1.wireOp",EDGE,"E46.2.26"),sQuery(id+"F1.wireOp",EDGE,"E46.2.28"),sQuery(id+"F1.wireOp",EDGE,"E46.2.29"),sQuery(id+"F1.wireOp",EDGE,"E46.3.0"),sQuery(id+"F1.wireOp",EDGE,"E46.3.1"),sQuery(id+"F1.wireOp",EDGE,"E46.3.2"),sQuery(id+"F1.wireOp",EDGE,"E46.3.3"),sQuery(id+"F1.wireOp",EDGE,"E46.3.4"),sQuery(id+"F1.wireOp",EDGE,"E46.3.5"),sQuery(id+"F1.wireOp",EDGE,"E46.3.7"),sQuery(id+"F1.wireOp",EDGE,"E46.3.8"),sQuery(id+"F1.wireOp",EDGE,"E46.3.11"),sQuery(id+"F1.wireOp",EDGE,"E46.3.12"),sQuery(id+"F1.wireOp",EDGE,"E46.3.13"),sQuery(id+"F1.wireOp",EDGE,"E46.3.14"),sQuery(id+"F1.wireOp",EDGE,"E46.3.15"),sQuery(id+"F1.wireOp",EDGE,"E46.3.16"),sQuery(id+"F1.wireOp",EDGE,"E46.3.17"),sQuery(id+"F1.wireOp",EDGE,"E46.3.19"),sQuery(id+"F1.wireOp",EDGE,"E46.3.20"),sQuery(id+"F1.wireOp",EDGE,"E46.3.21"),sQuery(id+"F1.wireOp",EDGE,"E46.3.22"),sQuery(id+"F1.wireOp",EDGE,"E46.3.26"),sQuery(id+"F1.wireOp",EDGE,"E46.3.28"),sQuery(id+"F1.wireOp",EDGE,"E46.3.29"),sQuery(id+"F1.wireOp",EDGE,"E46.4.0"),sQuery(id+"F1.wireOp",EDGE,"E46.4.1"),sQuery(id+"F1.wireOp",EDGE,"E46.4.2"),sQuery(id+"F1.wireOp",EDGE,"E46.4.3"),sQuery(id+"F1.wireOp",EDGE,"E46.4.4"),sQuery(id+"F1.wireOp",EDGE,"E46.4.5"),sQuery(id+"F1.wireOp",EDGE,"E46.4.7"),sQuery(id+"F1.wireOp",EDGE,"E46.4.8"),sQuery(id+"F1.wireOp",EDGE,"E46.4.11"),sQuery(id+"F1.wireOp",EDGE,"E46.4.12"),sQuery(id+"F1.wireOp",EDGE,"E46.4.13"),sQuery(id+"F1.wireOp",EDGE,"E46.4.14"),sQuery(id+"F1.wireOp",EDGE,"E46.4.15"),sQuery(id+"F1.wireOp",EDGE,"E46.4.16"),sQuery(id+"F1.wireOp",EDGE,"E46.4.17"),sQuery(id+"F1.wireOp",EDGE,"E46.4.19"),sQuery(id+"F1.wireOp",EDGE,"E46.4.20"),sQuery(id+"F1.wireOp",EDGE,"E46.4.21"),sQuery(id+"F1.wireOp",EDGE,"E46.4.22"),sQuery(id+"F1.wireOp",EDGE,"E46.4.26"),sQuery(id+"F1.wireOp",EDGE,"E46.4.28"),sQuery(id+"F1.wireOp",EDGE,"E46.4.29"),sQuery(id+"F1.wireOp",EDGE,"E46.5.0"),sQuery(id+"F1.wireOp",EDGE,"E46.5.1"),sQuery(id+"F1.wireOp",EDGE,"E46.5.2"),sQuery(id+"F1.wireOp",EDGE,"E46.5.3"),sQuery(id+"F1.wireOp",EDGE,"E46.5.4"),sQuery(id+"F1.wireOp",EDGE,"E46.5.5"),sQuery(id+"F1.wireOp",EDGE,"E46.5.7"),sQuery(id+"F1.wireOp",EDGE,"E46.5.8"),sQuery(id+"F1.wireOp",EDGE,"E46.5.11"),sQuery(id+"F1.wireOp",EDGE,"E46.5.12"),sQuery(id+"F1.wireOp",EDGE,"E46.5.13"),sQuery(id+"F1.wireOp",EDGE,"E46.5.14"),sQuery(id+"F1.wireOp",EDGE,"E46.5.15"),sQuery(id+"F1.wireOp",EDGE,"E46.5.16"),sQuery(id+"F1.wireOp",EDGE,"E46.5.17"),sQuery(id+"F1.wireOp",EDGE,"E46.5.19"),sQuery(id+"F1.wireOp",EDGE,"E46.5.20"),sQuery(id+"F1.wireOp",EDGE,"E46.5.21"),sQuery(id+"F1.wireOp",EDGE,"E46.5.22"),sQuery(id+"F1.wireOp",EDGE,"E46.5.26"),sQuery(id+"F1.wireOp",EDGE,"E46.5.28"),sQuery(id+"F1.wireOp",EDGE,"E46.5.29"),sQuery(id+"F1.wireOp",EDGE,"E47"),sQuery(id+"F1.wireOp",EDGE,"E48"),sQuery(id+"F1.wireOp",EDGE,"E49"),sQuery(id+"F1.wireOp",EDGE,"E50"),sQuery(id+"F1.wireOp",EDGE,"E51"),sQuery(id+"F1.wireOp",EDGE,"E52")])]});
            booleanBodies(context, id + "F4", {"operationType" : BooleanOperationType.INTERSECTION, "tools" : qUnion([Q0, Q1]), "keepTools" : true});
        }
        {
            var Q0;
            Q0=makeQuery(id+"F3.opExtrude","SWEPT_BODY",BODY,{"disambiguationData":[OSD([sQuery(id+"F1.wireOp",EDGE,"E12.0"),sQuery(id+"F1.wireOp",EDGE,"E12.1"),sQuery(id+"F1.wireOp",EDGE,"E12.2"),sQuery(id+"F1.wireOp",EDGE,"E12.3"),sQuery(id+"F1.wireOp",EDGE,"E12.4"),sQuery(id+"F1.wireOp",EDGE,"E12.5"),sQuery(id+"F1.wireOp",EDGE,"E15.trimOffspring"),sQuery(id+"F1.wireOp",EDGE,"E18"),sQuery(id+"F1.wireOp",EDGE,"E20"),sQuery(id+"F1.wireOp",EDGE,"E22"),sQuery(id+"F1.wireOp",EDGE,"E23.0"),sQuery(id+"F1.wireOp",EDGE,"E24.MirrorCS"),sQuery(id+"F1.wireOp",EDGE,"E25"),sQuery(id+"F1.wireOp",EDGE,"E26"),sQuery(id+"F1.wireOp",EDGE,"E29.MirrorCS"),sQuery(id+"F1.wireOp",EDGE,"E30"),sQuery(id+"F1.wireOp",EDGE,"E31"),sQuery(id+"F1.wireOp",EDGE,"E32.MirrorCS"),sQuery(id+"F1.wireOp",EDGE,"E33.MirrorCS"),sQuery(id+"F1.wireOp",EDGE,"E34.MirrorCS"),sQuery(id+"F1.wireOp",EDGE,"E35.MirrorCS"),sQuery(id+"F1.wireOp",EDGE,"E36.MirrorCS"),sQuery(id+"F1.wireOp",EDGE,"E37.MirrorCS"),sQuery(id+"F1.wireOp",EDGE,"E39.MirrorCS"),sQuery(id+"F1.wireOp",EDGE,"E40.MirrorCS"),sQuery(id+"F1.wireOp",EDGE,"E41.MirrorCS"),sQuery(id+"F1.wireOp",EDGE,"E42.MirrorCS"),sQuery(id+"F1.wireOp",EDGE,"E45.MirrorCS"),sQuery(id+"F1.wireOp",EDGE,"E46.1.0"),sQuery(id+"F1.wireOp",EDGE,"E46.1.1"),sQuery(id+"F1.wireOp",EDGE,"E46.1.2"),sQuery(id+"F1.wireOp",EDGE,"E46.1.3"),sQuery(id+"F1.wireOp",EDGE,"E46.1.4"),sQuery(id+"F1.wireOp",EDGE,"E46.1.5"),sQuery(id+"F1.wireOp",EDGE,"E46.1.7"),sQuery(id+"F1.wireOp",EDGE,"E46.1.8"),sQuery(id+"F1.wireOp",EDGE,"E46.1.11"),sQuery(id+"F1.wireOp",EDGE,"E46.1.12"),sQuery(id+"F1.wireOp",EDGE,"E46.1.13"),sQuery(id+"F1.wireOp",EDGE,"E46.1.14"),sQuery(id+"F1.wireOp",EDGE,"E46.1.15"),sQuery(id+"F1.wireOp",EDGE,"E46.1.16"),sQuery(id+"F1.wireOp",EDGE,"E46.1.17"),sQuery(id+"F1.wireOp",EDGE,"E46.1.19"),sQuery(id+"F1.wireOp",EDGE,"E46.1.20"),sQuery(id+"F1.wireOp",EDGE,"E46.1.21"),sQuery(id+"F1.wireOp",EDGE,"E46.1.22"),sQuery(id+"F1.wireOp",EDGE,"E46.1.26"),sQuery(id+"F1.wireOp",EDGE,"E46.1.28"),sQuery(id+"F1.wireOp",EDGE,"E46.1.29"),sQuery(id+"F1.wireOp",EDGE,"E46.2.0"),sQuery(id+"F1.wireOp",EDGE,"E46.2.1"),sQuery(id+"F1.wireOp",EDGE,"E46.2.2"),sQuery(id+"F1.wireOp",EDGE,"E46.2.3"),sQuery(id+"F1.wireOp",EDGE,"E46.2.4"),sQuery(id+"F1.wireOp",EDGE,"E46.2.5"),sQuery(id+"F1.wireOp",EDGE,"E46.2.7"),sQuery(id+"F1.wireOp",EDGE,"E46.2.8"),sQuery(id+"F1.wireOp",EDGE,"E46.2.11"),sQuery(id+"F1.wireOp",EDGE,"E46.2.12"),sQuery(id+"F1.wireOp",EDGE,"E46.2.13"),sQuery(id+"F1.wireOp",EDGE,"E46.2.14"),sQuery(id+"F1.wireOp",EDGE,"E46.2.15"),sQuery(id+"F1.wireOp",EDGE,"E46.2.16"),sQuery(id+"F1.wireOp",EDGE,"E46.2.17"),sQuery(id+"F1.wireOp",EDGE,"E46.2.19"),sQuery(id+"F1.wireOp",EDGE,"E46.2.20"),sQuery(id+"F1.wireOp",EDGE,"E46.2.21"),sQuery(id+"F1.wireOp",EDGE,"E46.2.22"),sQuery(id+"F1.wireOp",EDGE,"E46.2.26"),sQuery(id+"F1.wireOp",EDGE,"E46.2.28"),sQuery(id+"F1.wireOp",EDGE,"E46.2.29"),sQuery(id+"F1.wireOp",EDGE,"E46.3.0"),sQuery(id+"F1.wireOp",EDGE,"E46.3.1"),sQuery(id+"F1.wireOp",EDGE,"E46.3.2"),sQuery(id+"F1.wireOp",EDGE,"E46.3.3"),sQuery(id+"F1.wireOp",EDGE,"E46.3.4"),sQuery(id+"F1.wireOp",EDGE,"E46.3.5"),sQuery(id+"F1.wireOp",EDGE,"E46.3.7"),sQuery(id+"F1.wireOp",EDGE,"E46.3.8"),sQuery(id+"F1.wireOp",EDGE,"E46.3.11"),sQuery(id+"F1.wireOp",EDGE,"E46.3.12"),sQuery(id+"F1.wireOp",EDGE,"E46.3.13"),sQuery(id+"F1.wireOp",EDGE,"E46.3.14"),sQuery(id+"F1.wireOp",EDGE,"E46.3.15"),sQuery(id+"F1.wireOp",EDGE,"E46.3.16"),sQuery(id+"F1.wireOp",EDGE,"E46.3.17"),sQuery(id+"F1.wireOp",EDGE,"E46.3.19"),sQuery(id+"F1.wireOp",EDGE,"E46.3.20"),sQuery(id+"F1.wireOp",EDGE,"E46.3.21"),sQuery(id+"F1.wireOp",EDGE,"E46.3.22"),sQuery(id+"F1.wireOp",EDGE,"E46.3.26"),sQuery(id+"F1.wireOp",EDGE,"E46.3.28"),sQuery(id+"F1.wireOp",EDGE,"E46.3.29"),sQuery(id+"F1.wireOp",EDGE,"E46.4.0"),sQuery(id+"F1.wireOp",EDGE,"E46.4.1"),sQuery(id+"F1.wireOp",EDGE,"E46.4.2"),sQuery(id+"F1.wireOp",EDGE,"E46.4.3"),sQuery(id+"F1.wireOp",EDGE,"E46.4.4"),sQuery(id+"F1.wireOp",EDGE,"E46.4.5"),sQuery(id+"F1.wireOp",EDGE,"E46.4.7"),sQuery(id+"F1.wireOp",EDGE,"E46.4.8"),sQuery(id+"F1.wireOp",EDGE,"E46.4.11"),sQuery(id+"F1.wireOp",EDGE,"E46.4.12"),sQuery(id+"F1.wireOp",EDGE,"E46.4.13"),sQuery(id+"F1.wireOp",EDGE,"E46.4.14"),sQuery(id+"F1.wireOp",EDGE,"E46.4.15"),sQuery(id+"F1.wireOp",EDGE,"E46.4.16"),sQuery(id+"F1.wireOp",EDGE,"E46.4.17"),sQuery(id+"F1.wireOp",EDGE,"E46.4.19"),sQuery(id+"F1.wireOp",EDGE,"E46.4.20"),sQuery(id+"F1.wireOp",EDGE,"E46.4.21"),sQuery(id+"F1.wireOp",EDGE,"E46.4.22"),sQuery(id+"F1.wireOp",EDGE,"E46.4.26"),sQuery(id+"F1.wireOp",EDGE,"E46.4.28"),sQuery(id+"F1.wireOp",EDGE,"E46.4.29"),sQuery(id+"F1.wireOp",EDGE,"E46.5.0"),sQuery(id+"F1.wireOp",EDGE,"E46.5.1"),sQuery(id+"F1.wireOp",EDGE,"E46.5.2"),sQuery(id+"F1.wireOp",EDGE,"E46.5.3"),sQuery(id+"F1.wireOp",EDGE,"E46.5.4"),sQuery(id+"F1.wireOp",EDGE,"E46.5.5"),sQuery(id+"F1.wireOp",EDGE,"E46.5.7"),sQuery(id+"F1.wireOp",EDGE,"E46.5.8"),sQuery(id+"F1.wireOp",EDGE,"E46.5.11"),sQuery(id+"F1.wireOp",EDGE,"E46.5.12"),sQuery(id+"F1.wireOp",EDGE,"E46.5.13"),sQuery(id+"F1.wireOp",EDGE,"E46.5.14"),sQuery(id+"F1.wireOp",EDGE,"E46.5.15"),sQuery(id+"F1.wireOp",EDGE,"E46.5.16"),sQuery(id+"F1.wireOp",EDGE,"E46.5.17"),sQuery(id+"F1.wireOp",EDGE,"E46.5.19"),sQuery(id+"F1.wireOp",EDGE,"E46.5.20"),sQuery(id+"F1.wireOp",EDGE,"E46.5.21"),sQuery(id+"F1.wireOp",EDGE,"E46.5.22"),sQuery(id+"F1.wireOp",EDGE,"E46.5.26"),sQuery(id+"F1.wireOp",EDGE,"E46.5.28"),sQuery(id+"F1.wireOp",EDGE,"E46.5.29"),sQuery(id+"F1.wireOp",EDGE,"E47"),sQuery(id+"F1.wireOp",EDGE,"E48"),sQuery(id+"F1.wireOp",EDGE,"E49"),sQuery(id+"F1.wireOp",EDGE,"E50"),sQuery(id+"F1.wireOp",EDGE,"E51"),sQuery(id+"F1.wireOp",EDGE,"E52")])]});
            var Q1;
            Q1=makeQuery(id+"F2.opRevolve","SWEPT_BODY",BODY,{"disambiguationData":[OSD([sQuery(id+"F0.wireOp",EDGE,"E1"),sQuery(id+"F0.wireOp",EDGE,"E2"),sQuery(id+"F0.wireOp",EDGE,"E4.0"),sQuery(id+"F0.wireOp",EDGE,"E5"),sQuery(id+"F0.wireOp",EDGE,"E7.0")])]});
            booleanBodies(context, id + "F5", {"operationType" : BooleanOperationType.SUBTRACTION, "tools" : qUnion([Q0]), "targets" : qUnion([Q1])});
        }
    });
